# Revit family: Electronics_Commercial-Audio_Biamp_ ThinkSmart_Core
name_source: partatom
category: Communication Devices
units: mm (PartAtom-declared; Revit-internal decimal feet)

## family parameters
Cut with Voids When Loaded = No
Host = Face
Maintain Annotation Orientation = No
OmniClass Number = 23.85.00.00
OmniClass Title = Information and Communication
Part Type = Normal
Room Calculation Point = No
Round Connector Dimension = Use Diameter
Shared = No

## types (1)
- ThinkSmart Core
    Apparent Load = 90 VA
    Connector Description = Power supply
    Default Elevation = 1219 mm
    Depth = 200 mm  [stored 0.656168 ft]
    Description = Lenovo ThinkSmart™ Core
    Height = 38 mm
    Housing Material = Biamp - Metal - Black
    Installation Type 1 = Surface-Mount
    Installation Type 2 = Under-Table Mount
    Installation Type 3 = Wall-Mount
    Manufacturer = Biamp
    Max Power Consumption = 90 W
    Model = ThinkSmart Core
    Number of Poles = 1
    Power Factor = 1
    Product Documentation Link = https://downloads.biamp.com
    Product Page URL = https://www.biamp.com
    Product data url = https://bimobject.com
    URL = https://www.biamp.com
    Version = 1
    Voltage = 120 V
    Weight = 1.10 kgf
    Width = 226 mm  [stored 0.74147 ft]

note: [stored X ft] marks values corroborated as IEEE doubles in the binary element streams (Revit-internal decimal feet)

## geometry (parser evidence)
native form markers: Sweep x9
no freeform markers — native parametric forms only
